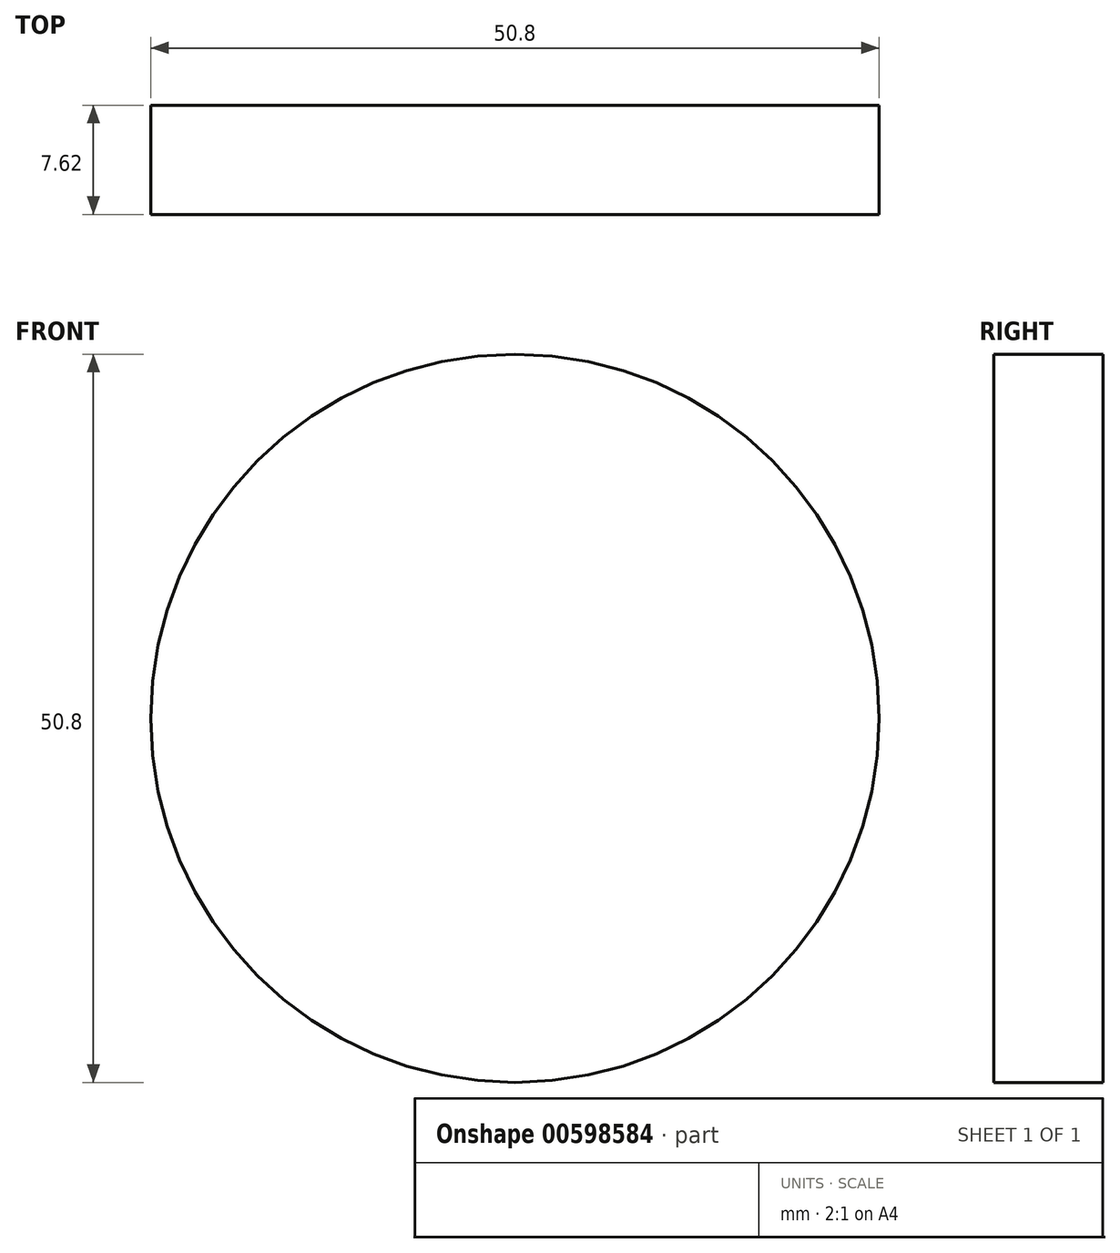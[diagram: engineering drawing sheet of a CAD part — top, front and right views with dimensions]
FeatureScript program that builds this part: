
annotation { "Feature Type Name" : "Feature", "Feature Type Description" : "" }
export const myFeature = defineFeature(function(context is Context, id is Id, definition is map)
    precondition{}
    {
        {
            var Q0;
            Q0=qCreatedBy(makeId("Front.planeOp"),FACE);
            var sketch = newSketch(context, id + "F0", { "sketchPlane" : qUnion([Q0])});
            skCircle(sketch, "E0", {"center": v(0, 0) * mm, "radius": 25.4 * mm});
            skSolve(sketch);
        }
        {
            var Q0;
            Q0=makeQuery(id+"F0.imprint","IMPRINT",FACE,{"disambiguationData":[TD([[makeQuery(id+"F0.imprint","IMPRINT",EDGE,{"derivedFrom":sQuery(id+"F0.wireOp",EDGE,"E0")}),1.0]])]});
            extrude(context, id + "F1", {"entities" : qUnion([Q0]), "depth" : 7.62 * mm, "offsetDistance" : 25.4 * mm});
        }
    });
